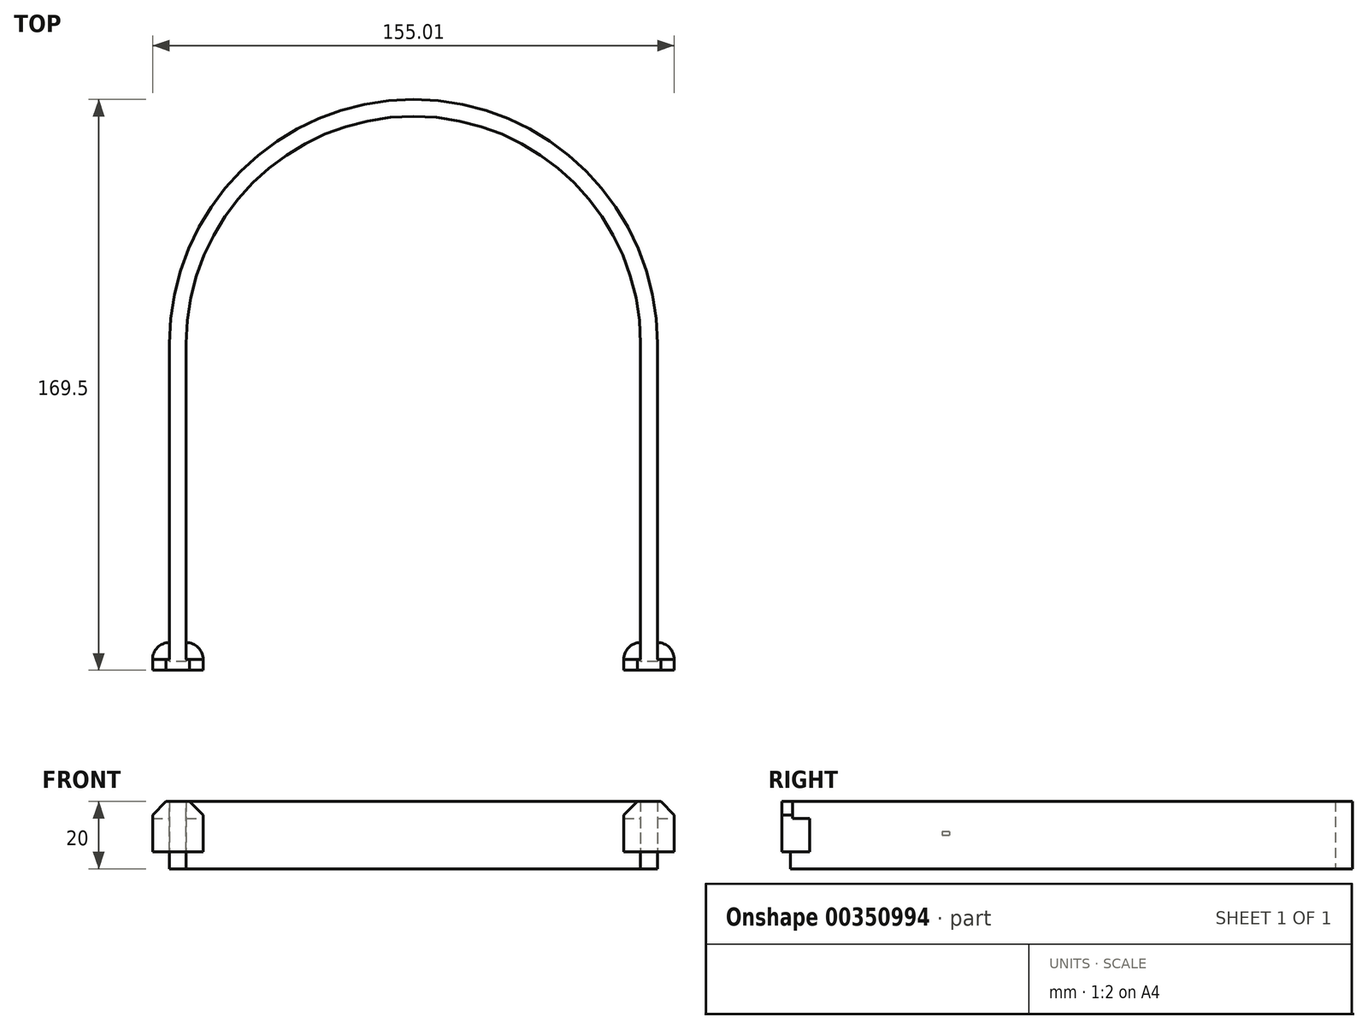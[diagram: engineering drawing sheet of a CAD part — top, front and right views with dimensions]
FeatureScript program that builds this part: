
annotation { "Feature Type Name" : "Feature", "Feature Type Description" : "" }
export const myFeature = defineFeature(function(context is Context, id is Id, definition is map)
    precondition{}
    {
        {
            var Q0;
            Q0=qCreatedBy(makeId("Top.planeOp"),FACE);
            var sketch = newSketch(context, id + "F0", { "sketchPlane" : qUnion([Q0])});
            skCircle(sketch, "E0", {"center": v(0, 0) * mm, "radius": 67.5 * mm});
            skLineSegment(sketch, "E1", {"start": v(0, -67.5) * mm, "end": v(0, -89.5) * mm});
            skLineSegment(sketch, "E2", {"start": v(0, -89.5) * mm, "end": v(-67.5, -89.5) * mm});
            skLineSegment(sketch, "E3", {"start": v(0, -89.5) * mm, "end": v(67.5, -89.5) * mm});
            skLineSegment(sketch, "E4", {"start": v(-67.5, -89.5) * mm, "end": v(-67.5, 0) * mm});
            skLineSegment(sketch, "E5", {"start": v(67.5, -89.5) * mm, "end": v(67.5, 0) * mm});
            skCircle(sketch, "E6", {"center": v(0, 0) * mm, "radius": 72.5 * mm});
            skLineSegment(sketch, "E7", {"start": v(-67.5, -89.5) * mm, "end": v(-72.5, -89.5) * mm});
            skLineSegment(sketch, "E8", {"start": v(-67.5, -89.5) * mm, "end": v(-67.5, -94.5) * mm});
            skLineSegment(sketch, "E9", {"start": v(-72.5, -89.5) * mm, "end": v(-72.5, 0) * mm});
            skLineSegment(sketch, "E10", {"start": v(-67.5, -94.5) * mm, "end": v(67.5, -94.5) * mm});
            skLineSegment(sketch, "E11", {"start": v(67.5, -94.5) * mm, "end": v(67.5, -89.5) * mm});
            skLineSegment(sketch, "E12", {"start": v(67.5, -89.5) * mm, "end": v(72.5, -89.5) * mm});
            skLineSegment(sketch, "E13", {"start": v(67.5, -94.5) * mm, "end": v(72.5, -94.5) * mm});
            skLineSegment(sketch, "E14", {"start": v(72.5, -94.5) * mm, "end": v(72.5, -89.5) * mm});
            skLineSegment(sketch, "E15", {"start": v(72.5, -89.5) * mm, "end": v(72.5, 0) * mm});
            skLineSegment(sketch, "E16", {"start": v(-72.5, -89.5) * mm, "end": v(-72.5, -94.5) * mm});
            skLineSegment(sketch, "E17", {"start": v(-72.5, -94.5) * mm, "end": v(-67.5, -94.5) * mm});
            skSolve(sketch);
        }
        {
            var Q0;
            Q0=makeQuery(id+"F0.imprint","IMPRINT",FACE,{"disambiguationData":[TD([[makeQuery(id+"F0.imprint","IMPRINT",EDGE,{"derivedFrom":sQuery(id+"F0.wireOp",EDGE,"E7")}),1.0]])]});
            var Q1;
            Q1=makeQuery(id+"F0.imprint","IMPRINT",FACE,{"disambiguationData":[TD([[makeQuery(id+"F0.imprint","IMPRINT",EDGE,{"derivedFrom":sQuery(id+"F0.wireOp",EDGE,"E11")}),-1.0]])]});
            var Q2;
            {var subQ0=sQuery(id+"F0.wireOp",EDGE,"E7");Q2=makeQuery(id+"F0.imprint","IMPRINT",FACE,{"disambiguationData":[TD([[makeQuery(id+"F0.imprint","IMPRINT",EDGE,{"derivedFrom":subQ0}),-1.0]])]});}
            var Q3;
            {var subQ0=sQuery(id+"F0.wireOp",EDGE,"E12");Q3=makeQuery(id+"F0.imprint","IMPRINT",FACE,{"disambiguationData":[TD([[makeQuery(id+"F0.imprint","IMPRINT",EDGE,{"derivedFrom":subQ0}),1.0]])]});}
            var Q4;
            {var subQ3=sQuery(id+"F0.wireOp",EDGE,"E4");var subQ4=sQuery(id+"F0.wireOp",EDGE,"E0");var subQ5=makeQuery(id+"F0.imprint","INTERSECT",VERTEX,{"derivedFrom":[subQ4,subQ3]});Q4=makeQuery(id+"F0.imprint","IMPRINT",FACE,{"disambiguationData":[TD([[makeQuery(id+"F0.imprint","IMPRINT",EDGE,{"disambiguationData":[TD([[subQ5,1.0]])],"derivedFrom":subQ4}),-1.0]])]});}
            extrude(context, id + "F1", {"entities" : qUnion([Q0, Q1, Q2, Q3, Q4]), "depth" : 20 * mm});
        }
        {
            var Q0;
            Q0=makeQuery(id+"F1.opExtrude","SWEPT_FACE",FACE,{"disambiguationData":[OSD([sQuery(id+"F0.wireOp",EDGE,"E9"),sQuery(id+"F0.wireOp",EDGE,"E16")])]});
            var sketch = newSketch(context, id + "F2", { "sketchPlane" : qUnion([Q0])});
            skLineSegment(sketch, "E18", {"start": v(47.25, 20) * mm, "end": v(47.25, 10) * mm});
            skPoint(sketch, "E18.endSnap0", {"position": v(47.25, 20) * mm});
            skLineSegment(sketch, "E19", {"start": v(47.25, 10) * mm, "end": v(47.25, 11.06) * mm});
            skLineSegment(sketch, "E20", {"start": v(47.25, 11.06) * mm, "end": v(49.43, 11.06) * mm});
            skLineSegment(sketch, "E21", {"start": v(49.43, 11.06) * mm, "end": v(49.43, 10) * mm});
            skLineSegment(sketch, "E22", {"start": v(49.43, 10) * mm, "end": v(47.25, 10) * mm});
            skSolve(sketch);
        }
        {
            var Q0;
            Q0 = qSketchRegion(id + "F2", true);
            extrude(context, id + "F3", {"entities" : qUnion([Q0]), "operationType" : NewBodyOperationType.ADD, "depth" : 0 * mm});
        }
        {
            var Q0;
            Q0=makeQuery(id+"F3.opExtrude","SWEPT_FACE",FACE,{"disambiguationData":[OSD([sQuery(id+"F2.wireOp",EDGE,"E22")])]});
            var sketch = newSketch(context, id + "F4", { "sketchPlane" : qUnion([Q0])});
            skLineSegment(sketch, "E23", {"start": v(-72.5, 94.5) * mm, "end": v(-77.5, 94.5) * mm});
            skLineSegment(sketch, "E24", {"start": v(-67.5, 94.5) * mm, "end": v(-62.5, 94.5) * mm});
            skLineSegment(sketch, "E25", {"start": v(-77.5, 94.5) * mm, "end": v(-77.5, 97) * mm});
            skLineSegment(sketch, "E26", {"start": v(-62.5, 94.5) * mm, "end": v(-62.5, 97) * mm});
            skLineSegment(sketch, "E27", {"start": v(-77.5, 97) * mm, "end": v(-62.5, 97) * mm});
            skLineSegment(sketch, "E28", {"start": v(-72.5, 94.5) * mm, "end": v(-67.5, 94.5) * mm});
            skLineSegment(sketch, "E29", {"start": v(67.51, 94.5) * mm, "end": v(62.51, 94.5) * mm});
            skLineSegment(sketch, "E30", {"start": v(72.51, 94.5) * mm, "end": v(77.51, 94.5) * mm});
            skLineSegment(sketch, "E31", {"start": v(62.51, 94.5) * mm, "end": v(62.51, 97) * mm});
            skLineSegment(sketch, "E32", {"start": v(77.51, 94.5) * mm, "end": v(77.51, 97) * mm});
            skLineSegment(sketch, "E33", {"start": v(62.51, 97) * mm, "end": v(77.51, 97) * mm});
            skLineSegment(sketch, "E34", {"start": v(67.51, 94.5) * mm, "end": v(72.51, 94.5) * mm});
            skLineSegment(sketch, "E35", {"start": v(-77.5, 94.5) * mm, "end": v(-77.5, 88.8) * mm});
            skLineSegment(sketch, "E36", {"start": v(-77.5, 88.8) * mm, "end": v(-62.5, 88.8) * mm});
            skLineSegment(sketch, "E37", {"start": v(-62.5, 88.8) * mm, "end": v(-62.5, 94.5) * mm});
            skLineSegment(sketch, "E38", {"start": v(62.51, 94.5) * mm, "end": v(62.51, 88.8) * mm});
            skLineSegment(sketch, "E39", {"start": v(62.51, 88.8) * mm, "end": v(77.51, 88.8) * mm});
            skLineSegment(sketch, "E40", {"start": v(77.51, 88.8) * mm, "end": v(77.51, 94.5) * mm});
            skSolve(sketch);
        }
        {
            var Q0;
            Q0 = qSketchRegion(id + "F4", true);
            extrude(context, id + "F5", {"entities" : qUnion([Q0]), "operationType" : NewBodyOperationType.ADD, "endBound" : BoundingType.SYMMETRIC, "oppositeDirection" : true, "depth" : 10 * mm});
        }
        {
            var Q0;
            Q0=makeQuery(id+"F5.opExtrude","SWEPT_EDGE",EDGE,{"disambiguationData":[OSD([sQuery(id+"F4.wireOp",EDGE,"E35"),sQuery(id+"F4.wireOp",EDGE,"E36")])]});
            var Q1;
            Q1=makeQuery(id+"F5.opExtrude","SWEPT_EDGE",EDGE,{"disambiguationData":[OSD([sQuery(id+"F4.wireOp",EDGE,"E39"),sQuery(id+"F4.wireOp",EDGE,"E40")])]});
            var Q2;
            Q2=makeQuery(id+"F5.opExtrude","SWEPT_EDGE",EDGE,{"disambiguationData":[OSD([sQuery(id+"F4.wireOp",EDGE,"E38"),sQuery(id+"F4.wireOp",EDGE,"E39")])]});
            var Q3;
            Q3=makeQuery(id+"F5.opExtrude","SWEPT_EDGE",EDGE,{"disambiguationData":[OSD([sQuery(id+"F4.wireOp",EDGE,"E36"),sQuery(id+"F4.wireOp",EDGE,"E37")])]});
            fillet(context, id + "F6", {"entities" : qUnion([Q0, Q1, Q2, Q3]), "radius" : 5 * mm, "tangentPropagation" : true, "allowEdgeOverflow" : false});
        }
        {
            var Q0;
            Q0=makeQuery(id+"F5.opExtrude","CAP_FACE",FACE,{"disambiguationData":[OSD([sQuery(id+"F4.wireOp",EDGE,"E25"),sQuery(id+"F4.wireOp",EDGE,"E26"),sQuery(id+"F4.wireOp",EDGE,"E27"),sQuery(id+"F4.wireOp",EDGE,"E35"),sQuery(id+"F4.wireOp",EDGE,"E36"),sQuery(id+"F4.wireOp",EDGE,"E37")])],"isStart":false});
            var sketch = newSketch(context, id + "F7", { "sketchPlane" : qUnion([Q0])});
            skLineSegment(sketch, "E41.bottom", {"start": v(-77.5, -97) * mm, "end": v(-62.5, -97) * mm});
            skLineSegment(sketch, "E41.top", {"start": v(-77.5, -93.8) * mm, "end": v(-62.5, -93.8) * mm});
            skLineSegment(sketch, "E41.left", {"start": v(-77.5, -97) * mm, "end": v(-77.5, -93.8) * mm});
            skLineSegment(sketch, "E41.right", {"start": v(-62.5, -97) * mm, "end": v(-62.5, -93.8) * mm});
            skSolve(sketch);
        }
        {
            var Q0;
            Q0 = qSketchRegion(id + "F7", true);
            extrude(context, id + "F8", {"entities" : qUnion([Q0]), "operationType" : NewBodyOperationType.ADD, "depth" : 5 * mm});
        }
        {
            var Q0;
            Q0=makeQuery(id+"F5.opExtrude","CAP_FACE",FACE,{"disambiguationData":[OSD([sQuery(id+"F4.wireOp",EDGE,"E31"),sQuery(id+"F4.wireOp",EDGE,"E32"),sQuery(id+"F4.wireOp",EDGE,"E33"),sQuery(id+"F4.wireOp",EDGE,"E38"),sQuery(id+"F4.wireOp",EDGE,"E39"),sQuery(id+"F4.wireOp",EDGE,"E40")])],"isStart":false});
            var sketch = newSketch(context, id + "F9", { "sketchPlane" : qUnion([Q0])});
            skLineSegment(sketch, "E42.bottom", {"start": v(62.51, -97) * mm, "end": v(77.51, -97) * mm});
            skLineSegment(sketch, "E42.top", {"start": v(62.51, -93.8) * mm, "end": v(77.51, -93.8) * mm});
            skLineSegment(sketch, "E42.left", {"start": v(62.51, -97) * mm, "end": v(62.51, -93.8) * mm});
            skLineSegment(sketch, "E42.right", {"start": v(77.51, -97) * mm, "end": v(77.51, -93.8) * mm});
            skSolve(sketch);
        }
        {
            var Q0;
            Q0 = qSketchRegion(id + "F9", true);
            extrude(context, id + "F10", {"entities" : qUnion([Q0]), "operationType" : NewBodyOperationType.ADD, "depth" : 5 * mm});
        }
        {
            var Q0;
            Q0=makeQuery(id+"F8.opExtrude","CAP_EDGE",EDGE,{"disambiguationData":[OSD([sQuery(id+"F7.wireOp",EDGE,"E41.left")])],"isStart":false});
            var Q1;
            Q1=makeQuery(id+"F10.opExtrude","CAP_EDGE",EDGE,{"disambiguationData":[OSD([sQuery(id+"F9.wireOp",EDGE,"E42.left")])],"isStart":false});
            var Q2;
            Q2=makeQuery(id+"F8.opExtrude","CAP_EDGE",EDGE,{"disambiguationData":[OSD([sQuery(id+"F7.wireOp",EDGE,"E41.right")])],"isStart":false});
            var Q3;
            Q3=makeQuery(id+"F10.opExtrude","CAP_EDGE",EDGE,{"disambiguationData":[OSD([sQuery(id+"F9.wireOp",EDGE,"E42.right")])],"isStart":false});
            chamfer(context, id + "F11", {"entities" : qUnion([Q0, Q1, Q2, Q3]), "width" : 4 * mm, "tangentPropagation" : true});
        }
    });
